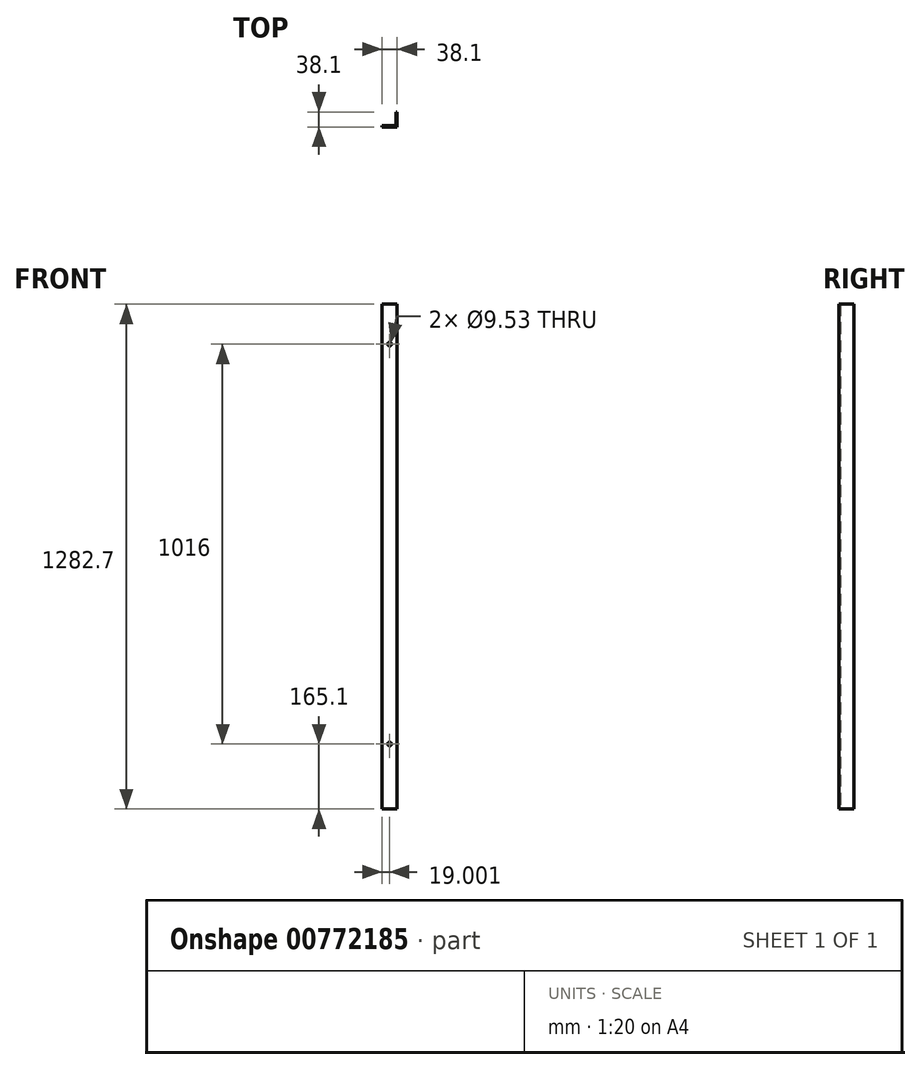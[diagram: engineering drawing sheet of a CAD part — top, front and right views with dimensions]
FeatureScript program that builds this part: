
annotation { "Feature Type Name" : "Feature", "Feature Type Description" : "" }
export const myFeature = defineFeature(function(context is Context, id is Id, definition is map)
    precondition{}
    {
        {
            var Q0;
            Q0=qCreatedBy(makeId("Top.planeOp"),FACE);
            var sketch = newSketch(context, id + "F0", { "sketchPlane" : qUnion([Q0])});
            skLineSegment(sketch, "E0", {"start": v(0, 0) * mm, "end": v(38.1, 0) * mm});
            skLineSegment(sketch, "E1", {"start": v(38.1, 0) * mm, "end": v(38.1, 38.1) * mm});
            skLineSegment(sketch, "E2", {"start": v(38.1, 38.1) * mm, "end": v(34.93, 38.1) * mm});
            skLineSegment(sketch, "E3", {"start": v(34.93, 38.1) * mm, "end": v(34.93, 3.18) * mm});
            skLineSegment(sketch, "E4", {"start": v(34.93, 3.18) * mm, "end": v(0, 3.18) * mm});
            skLineSegment(sketch, "E5", {"start": v(0, 3.18) * mm, "end": v(0, 0) * mm});
            skSolve(sketch);
        }
        {
            var Q0;
            Q0=makeQuery(id+"F0.imprint","IMPRINT",FACE,{"disambiguationData":[TD([[makeQuery(id+"F0.imprint","IMPRINT",EDGE,{"derivedFrom":sQuery(id+"F0.wireOp",EDGE,"E0")}),1.0]])]});
            extrude(context, id + "F1", {"entities" : qUnion([Q0]), "depth" : 1282.7 * mm, "offsetDistance" : 25.4 * mm});
        }
        {
            var Q0;
            Q0=makeQuery(id+"F1.opExtrude","SWEPT_FACE",FACE,{"disambiguationData":[OSD([sQuery(id+"F0.wireOp",EDGE,"E0")])]});
            var sketch = newSketch(context, id + "F2", { "sketchPlane" : qUnion([Q0])});
            skCircle(sketch, "E6", {"center": v(19, 1181.1) * mm, "radius": 4.76 * mm});
            skCircle(sketch, "E7", {"center": v(19, 165.1) * mm, "radius": 4.76 * mm});
            skSolve(sketch);
        }
        {
            var Q0;
            Q0=makeQuery(id+"F2.imprint","IMPRINT",FACE,{"disambiguationData":[TD([[makeQuery(id+"F2.imprint","IMPRINT",EDGE,{"derivedFrom":sQuery(id+"F2.wireOp",EDGE,"E6")}),1.0]])]});
            var Q1;
            Q1=makeQuery(id+"F2.imprint","IMPRINT",FACE,{"disambiguationData":[TD([[makeQuery(id+"F2.imprint","IMPRINT",EDGE,{"derivedFrom":sQuery(id+"F2.wireOp",EDGE,"E7")}),1.0]])]});
            extrude(context, id + "F3", {"entities" : qUnion([Q0, Q1]), "operationType" : NewBodyOperationType.REMOVE, "endBound" : BoundingType.THROUGH_ALL, "oppositeDirection" : true, "depth" : 25.4 * mm, "offsetDistance" : 25.4 * mm});
        }
    });
